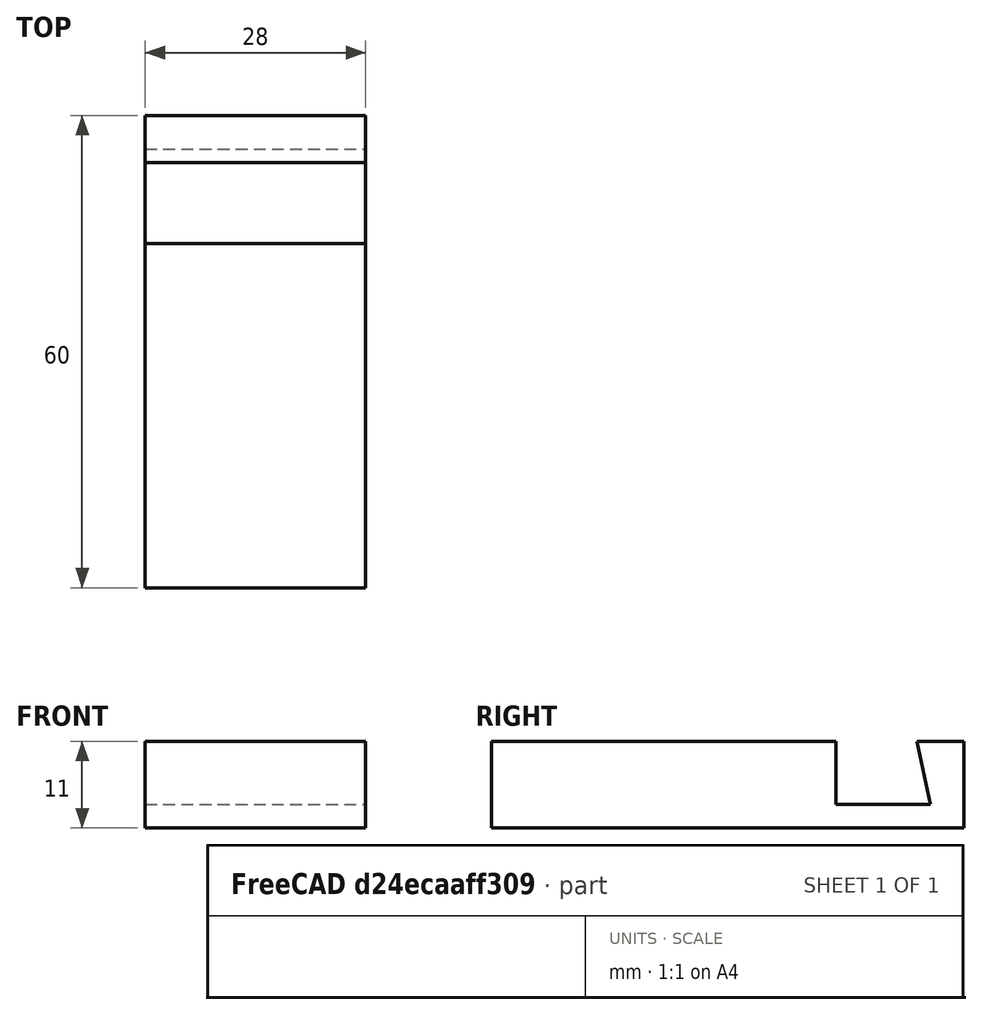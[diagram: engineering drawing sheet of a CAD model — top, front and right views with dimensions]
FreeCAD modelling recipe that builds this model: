
FCSTD DOCUMENT  (FreeCAD 1.0R38806 (Git))
Label: soporte
License: All rights reserved
LicenseURL: https://en.wikipedia.org/wiki/All_rights_reserved
objects: Sketcher::SketchObject×1, Part::Extrusion×1
note: 3 computed .brp shape members not serialized (recipe doc carries the construction recipe); baked Part::Feature solids carry a one-line shape summary decoded from their .brp

FEATURE [Sketcher::SketchObject] Sketch
  ArcFitTolerance = 1e-06
  FullyConstrained = false
  MakeInternals = false
  Placement = pos=(0,0,0) rot=(0.57735,0.57735,0.57735;2.0944rad)
  sketch-geometry (9):
    g0: LineSegment StartX=0 StartY=0 StartZ=0 EndX=0 EndY=11 EndZ=0
    g1: LineSegment StartX=0 StartY=11 StartZ=0 EndX=43.7638 EndY=11 EndZ=0
    g2: LineSegment StartX=43.7638 StartY=11 StartZ=0 EndX=43.7638 EndY=3 EndZ=0
    g3: LineSegment StartX=43.7638 StartY=3 StartZ=0 EndX=55.7638 EndY=3 EndZ=0
    g4: LineSegment StartX=55.7638 StartY=3 StartZ=0 EndX=54 EndY=11 EndZ=0
    g5: LineSegment StartX=54 StartY=11 StartZ=0 EndX=60 EndY=11 EndZ=0
    g6: LineSegment StartX=60 StartY=11 StartZ=0 EndX=60 EndY=0 EndZ=0
    g7: LineSegment StartX=60 StartY=0 StartZ=0 EndX=0 EndY=0 EndZ=0
    g8: LineSegment StartX=0 StartY=0 StartZ=0 EndX=0 EndY=11 EndZ=0
  constraints (24):
    c: Coincident(g-1,g0)
    c: PointOnObject(g0,g-2)
    c: Coincident(g0,g1)
    c: Horizontal(g1)
    c: Coincident(g1,g2)
    c: Vertical(g2)
    c: Coincident(g2,g3)
    c: Horizontal(g3)
    c: Coincident(g3,g4)
    c: Coincident(g4,g5)
    c: Horizontal(g5)
    c: Coincident(g5,g6)
    c: PointOnObject(g6,g-1)
    c: Vertical(g6)
    c: Coincident(g6,g7)
    c: Coincident(g7,g0)
    c: Coincident(g0,g8)
    c: Coincident(g8,g0)
    c: Equal(g0,g6)
    c: Distance(g0,g0) = 11
    c: Distance(g7,g7) = 60
    c: Distance(g3,g3) = 12
    c: Distance(g5,g5) = 6
    c: Distance(g2,g2) = 8
FEATURE [Part::Extrusion] Extrude
  Base = -> Sketch
  Dir = (1,0,0)
  DirMode = 2
  FaceMakerClass = Part::FaceMakerBullseye
  FaceMakerMode = 3
  LengthFwd = 28
  LengthRev = 0
  Solid = false
  Symmetric = false
